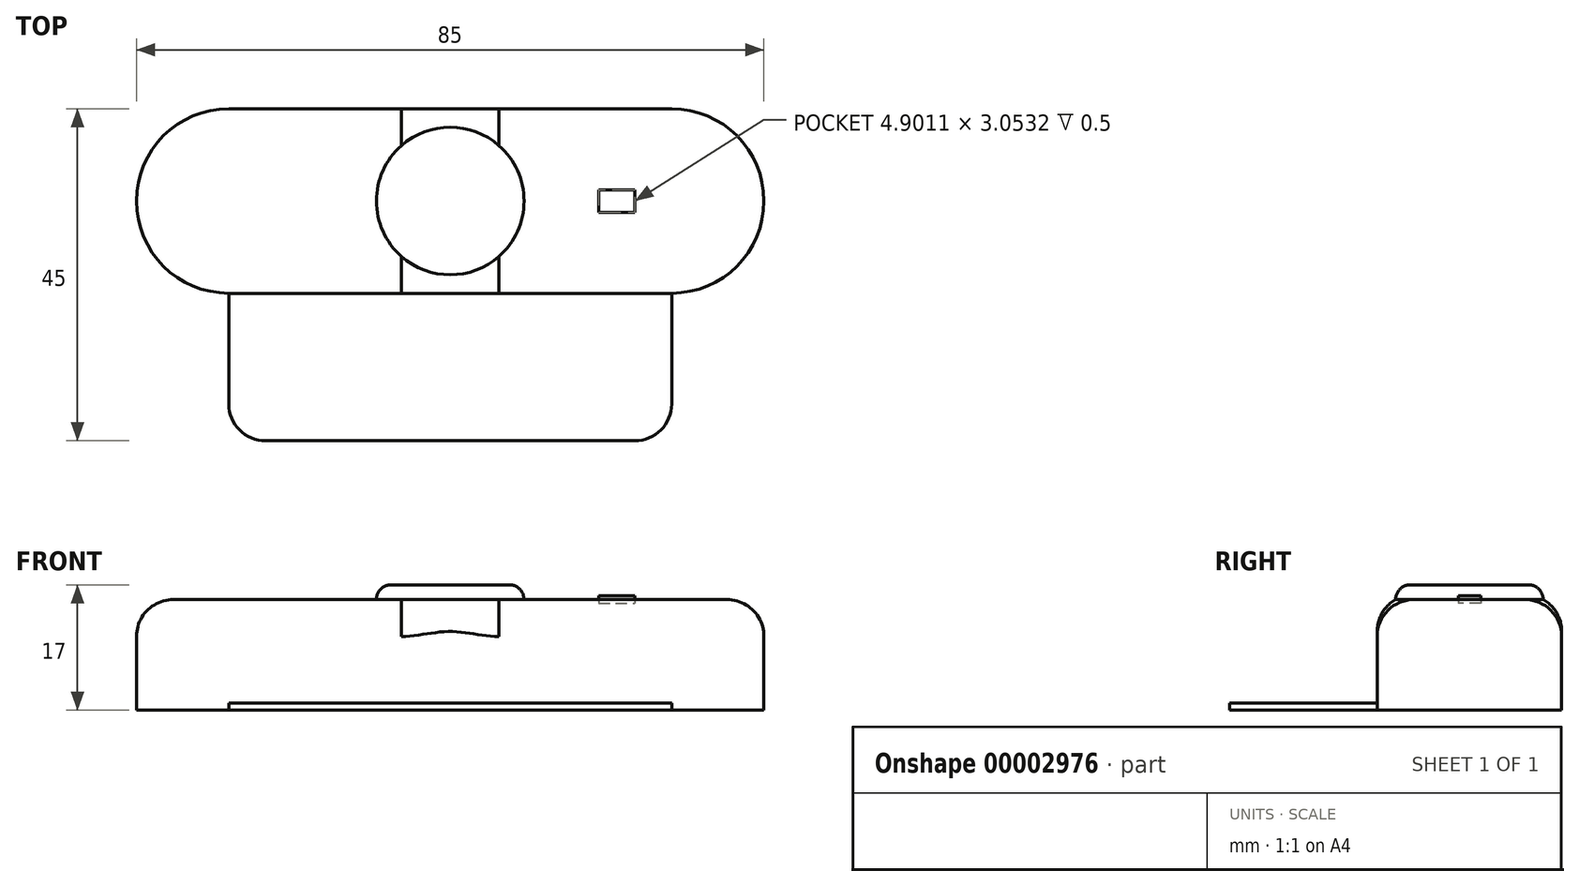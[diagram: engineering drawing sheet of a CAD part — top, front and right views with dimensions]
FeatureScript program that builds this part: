
annotation { "Feature Type Name" : "Feature", "Feature Type Description" : "" }
export const myFeature = defineFeature(function(context is Context, id is Id, definition is map)
    precondition{}
    {
        {
            var Q0;
            Q0=qCreatedBy(makeId("Top.planeOp"),FACE);
            var sketch = newSketch(context, id + "F0", { "sketchPlane" : qUnion([Q0])});
            skLineSegment(sketch, "E0.bottom", {"start": v(0, 0) * mm, "end": v(60, 0) * mm});
            skLineSegment(sketch, "E0.top", {"start": v(0, -25) * mm, "end": v(60, -25) * mm});
            skArc(sketch, "E1", {"start": v(0, 0) * mm, "mid": v(-12.5, -12.5) * mm, "end": v(0, -25) * mm});
            skArc(sketch, "E2", {"start": v(60, -25) * mm, "mid": v(72.5, -12.5) * mm, "end": v(60, 0) * mm});
            skSolve(sketch);
        }
        {
            var Q0;
            Q0=makeQuery(id+"F0.imprint","IMPRINT",FACE,{"disambiguationData":[TD([[makeQuery(id+"F0.imprint","IMPRINT",EDGE,{"derivedFrom":sQuery(id+"F0.wireOp",EDGE,"E0.bottom")}),-1.0]])]});
            extrude(context, id + "F1", {"entities" : qUnion([Q0]), "depth" : 15 * mm});
        }
        {
            var Q0;
            Q0=makeQuery(id+"F1.opExtrude","CAP_FACE",FACE,{"disambiguationData":[OSD([sQuery(id+"F0.wireOp",EDGE,"E0.bottom"),sQuery(id+"F0.wireOp",EDGE,"E0.top"),sQuery(id+"F0.wireOp",EDGE,"E1"),sQuery(id+"F0.wireOp",EDGE,"E2")])],"isStart":false});
            var sketch = newSketch(context, id + "F2", { "sketchPlane" : qUnion([Q0])});
            skCircle(sketch, "E3", {"center": v(30, -12.5) * mm, "radius": 10 * mm});
            skLineSegment(sketch, "E4", {"start": v(-12.5, -12.5) * mm, "end": v(72.5, -12.5) * mm, "construction": true});
            skLineSegment(sketch, "E5", {"start": v(30, 0) * mm, "end": v(30, -25) * mm, "construction": true});
            skSolve(sketch);
        }
        {
            var Q0;
            Q0=makeQuery(id+"F2.imprint","IMPRINT",FACE,{"disambiguationData":[TD([[makeQuery(id+"F2.imprint","IMPRINT",EDGE,{"derivedFrom":sQuery(id+"F2.wireOp",EDGE,"E3")}),1.0]])]});
            extrude(context, id + "F3", {"entities" : qUnion([Q0]), "operationType" : NewBodyOperationType.ADD, "depth" : 2 * mm});
        }
        {
            var Q0;
            Q0=makeQuery(id+"F1.opExtrude","CAP_FACE",FACE,{"disambiguationData":[OSD([sQuery(id+"F0.wireOp",EDGE,"E0.bottom"),sQuery(id+"F0.wireOp",EDGE,"E0.top"),sQuery(id+"F0.wireOp",EDGE,"E1"),sQuery(id+"F0.wireOp",EDGE,"E2")])],"isStart":false});
            var sketch = newSketch(context, id + "F4", { "sketchPlane" : qUnion([Q0])});
            skLineSegment(sketch, "E6.bottom", {"start": v(50.13, -10.97) * mm, "end": v(55.03, -10.97) * mm});
            skLineSegment(sketch, "E6.top", {"start": v(50.13, -14.03) * mm, "end": v(55.03, -14.03) * mm});
            skLineSegment(sketch, "E6.left", {"start": v(50.13, -10.97) * mm, "end": v(50.13, -14.03) * mm});
            skLineSegment(sketch, "E6.right", {"start": v(55.03, -10.97) * mm, "end": v(55.03, -14.03) * mm});
            skLineSegment(sketch, "E7", {"start": v(-12.5, -12.5) * mm, "end": v(72.5, -12.5) * mm, "construction": true});
            skLineSegment(sketch, "E8", {"start": v(30, 0) * mm, "end": v(30, -25) * mm, "construction": true});
            skLineSegment(sketch, "E9", {"start": v(50.13, -12.5) * mm, "end": v(55.03, -12.5) * mm, "construction": true});
            skSolve(sketch);
        }
        {
            var Q0;
            Q0=makeQuery(id+"F4.imprint","IMPRINT",FACE,{"disambiguationData":[TD([[makeQuery(id+"F4.imprint","IMPRINT",EDGE,{"derivedFrom":sQuery(id+"F4.wireOp",EDGE,"E6.bottom")}),-1.0]])]});
            extrude(context, id + "F5", {"entities" : qUnion([Q0]), "operationType" : NewBodyOperationType.REMOVE, "oppositeDirection" : true, "depth" : 0.5 * mm});
        }
        {
            var Q0;
            Q0=makeQuery(id+"F1.opExtrude","CAP_EDGE",EDGE,{"disambiguationData":[OSD([sQuery(id+"F0.wireOp",EDGE,"E1")])],"isStart":false});
            fillet(context, id + "F6", {"entities" : qUnion([Q0]), "radius" : 5 * mm, "tangentPropagation" : true, "allowEdgeOverflow" : false});
        }
        {
            var Q0;
            Q0=makeQuery(id+"F3.opExtrude","CAP_EDGE",EDGE,{"disambiguationData":[OSD([sQuery(id+"F2.wireOp",EDGE,"E3")])],"isStart":false});
            fillet(context, id + "F7", {"entities" : qUnion([Q0]), "radius" : 2 * mm, "tangentPropagation" : true, "allowEdgeOverflow" : false});
        }
        {
            var Q0;
            Q0=makeQuery(id+"F1.opExtrude","CAP_FACE",FACE,{"disambiguationData":[OSD([sQuery(id+"F0.wireOp",EDGE,"E0.bottom"),sQuery(id+"F0.wireOp",EDGE,"E0.top"),sQuery(id+"F0.wireOp",EDGE,"E1"),sQuery(id+"F0.wireOp",EDGE,"E2")])],"isStart":true});
            var sketch = newSketch(context, id + "F8", { "sketchPlane" : qUnion([Q0])});
            skLineSegment(sketch, "E10.bottom", {"start": v(0, 25) * mm, "end": v(60, 25) * mm});
            skLineSegment(sketch, "E10.top", {"start": v(5, 45) * mm, "end": v(55, 45) * mm});
            skLineSegment(sketch, "E10.left", {"start": v(0, 25) * mm, "end": v(0, 40) * mm});
            skLineSegment(sketch, "E10.right", {"start": v(60, 25) * mm, "end": v(60, 40) * mm});
            skLineSegment(sketch, "E11.bottom", {"start": v(60, 25) * mm, "end": v(60, 25) * mm});
            skLineSegment(sketch, "E11.top", {"start": v(60, 25) * mm, "end": v(60, 25) * mm});
            skLineSegment(sketch, "E11.left", {"start": v(60, 25) * mm, "end": v(60, 25) * mm});
            skLineSegment(sketch, "E11.right", {"start": v(60, 25) * mm, "end": v(60, 25) * mm});
            skPoint(sketch, "E12.visualSharp", {"position": v(0, 45) * mm});
            skArc(sketch, "E12.filletArc", {"start": v(5, 45) * mm, "mid": v(1.46, 43.54) * mm, "end": v(0, 40) * mm});
            skPoint(sketch, "E13.visualSharp", {"position": v(60, 45) * mm});
            skArc(sketch, "E13.filletArc", {"start": v(60, 40) * mm, "mid": v(58.54, 43.54) * mm, "end": v(55, 45) * mm});
            skSolve(sketch);
        }
        {
            var Q0;
            Q0=makeQuery(id+"F8.imprint","IMPRINT",FACE,{"disambiguationData":[TD([[makeQuery(id+"F8.imprint","IMPRINT",EDGE,{"derivedFrom":sQuery(id+"F8.wireOp",EDGE,"E10.bottom")}),1.0]])]});
            extrude(context, id + "F9", {"entities" : qUnion([Q0]), "operationType" : NewBodyOperationType.ADD, "oppositeDirection" : true, "depth" : 1 * mm});
        }
        {
            var Q0;
            Q0=makeQuery(id+"F5.boolean.opBoolean","COPY",FACE,{"derivedFrom":makeQuery(id+"F5.opExtrude","CAP_FACE",FACE,{"disambiguationData":[OSD([sQuery(id+"F4.wireOp",EDGE,"E6.bottom"),sQuery(id+"F4.wireOp",EDGE,"E6.top"),sQuery(id+"F4.wireOp",EDGE,"E6.left"),sQuery(id+"F4.wireOp",EDGE,"E6.right")])],"isStart":false})});
            var sketch = newSketch(context, id + "F10", { "sketchPlane" : qUnion([Q0])});
            skLineSegment(sketch, "E14.bottom", {"start": v(50.13, -10.97) * mm, "end": v(55.03, -10.97) * mm});
            skLineSegment(sketch, "E14.top", {"start": v(50.13, -14.03) * mm, "end": v(55.03, -14.03) * mm});
            skLineSegment(sketch, "E14.left", {"start": v(50.13, -10.97) * mm, "end": v(50.13, -14.03) * mm});
            skLineSegment(sketch, "E14.right", {"start": v(55.03, -10.97) * mm, "end": v(55.03, -14.03) * mm});
            skSolve(sketch);
        }
        {
            var Q0;
            Q0=makeQuery(id+"F10.imprint","IMPRINT",FACE,{"disambiguationData":[TD([[makeQuery(id+"F10.imprint","IMPRINT",EDGE,{"derivedFrom":sQuery(id+"F10.wireOp",EDGE,"E14.bottom")}),-1.0]])]});
            extrude(context, id + "F11", {"entities" : qUnion([Q0]), "depth" : 1 * mm});
        }
    });
